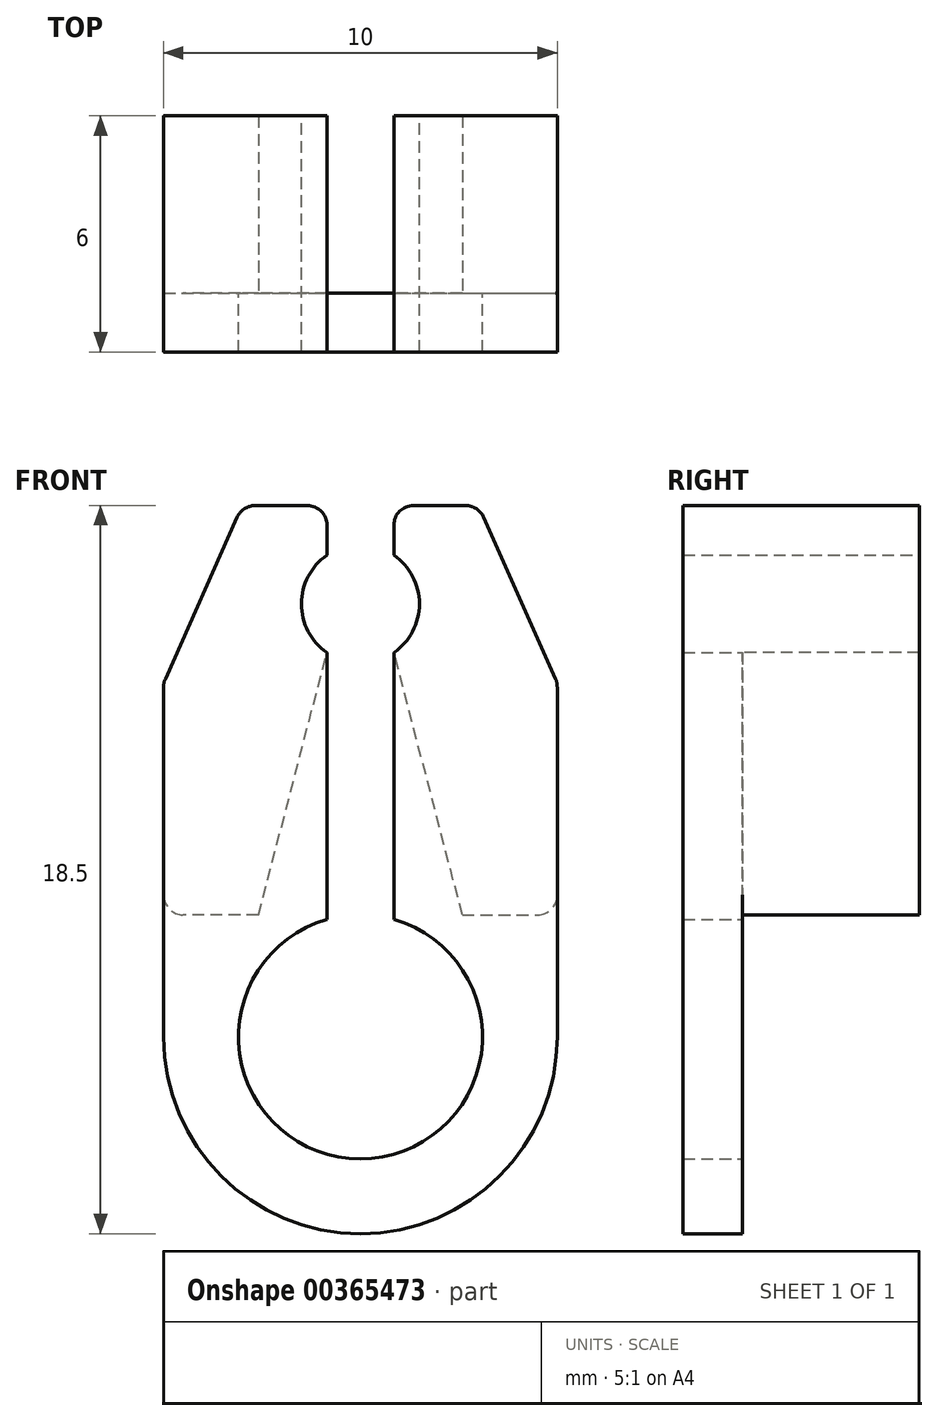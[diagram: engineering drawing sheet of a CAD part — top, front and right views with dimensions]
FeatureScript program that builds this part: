
annotation { "Feature Type Name" : "Feature", "Feature Type Description" : "" }
export const myFeature = defineFeature(function(context is Context, id is Id, definition is map)
    precondition{}
    {
        {
            var Q0;
            Q0=qCreatedBy(makeId("Front.planeOp"),FACE);
            var sketch = newSketch(context, id + "F0", { "sketchPlane" : qUnion([Q0])});
            skArc(sketch, "E0", {"start": v(-0.85, 2.98) * mm, "mid": v(0, -3.1) * mm, "end": v(0.85, 2.98) * mm});
            skArc(sketch, "E1", {"start": v(-0.85, 12.24) * mm, "mid": v(-1.5, 11) * mm, "end": v(-0.85, 9.76) * mm});
            skLineSegment(sketch, "E2", {"start": v(0, 12.5) * mm, "end": v(0, 13.5) * mm});
            skLineSegment(sketch, "E3", {"start": v(-0.85, 13.5) * mm, "end": v(-3, 13.5) * mm});
            skLineSegment(sketch, "E4", {"start": v(-5, 0) * mm, "end": v(-5, 9) * mm});
            skLineSegment(sketch, "E5", {"start": v(-5, 9) * mm, "end": v(-3, 13.5) * mm});
            skLineSegment(sketch, "E6.MirrorCS", {"start": v(5, 0) * mm, "end": v(5, 9) * mm});
            skLineSegment(sketch, "E7.MirrorCS", {"start": v(5, 9) * mm, "end": v(3, 13.5) * mm});
            skLineSegment(sketch, "E8.MirrorCS", {"start": v(0.85, 13.5) * mm, "end": v(3, 13.5) * mm});
            skLineSegment(sketch, "E9", {"start": v(-0.85, 2.98) * mm, "end": v(-0.85, 9.76) * mm});
            skLineSegment(sketch, "E10", {"start": v(0.85, 13.5) * mm, "end": v(0.85, 12.24) * mm});
            skArc(sketch, "E11.trimOffspring", {"start": v(-5, 0) * mm, "mid": v(0, -5) * mm, "end": v(5, 0) * mm});
            skPoint(sketch, "E12.orphan", {"position": v(0, 13.5) * mm});
            skLineSegment(sketch, "E13.trimOffspring", {"start": v(-0.85, 12.24) * mm, "end": v(-0.85, 13.5) * mm});
            skLineSegment(sketch, "E14.trimOffspring", {"start": v(0.85, 9.76) * mm, "end": v(0.85, 2.98) * mm});
            skArc(sketch, "E15.trimOffspring", {"start": v(0.85, 9.76) * mm, "mid": v(1.5, 11) * mm, "end": v(0.85, 12.24) * mm});
            skSolve(sketch);
        }
        {
            var Q0;
            Q0 = qSketchRegion(id + "F0", true);
            extrude(context, id + "F1", {"entities" : qUnion([Q0]), "depth" : 1.5 * mm});
        }
        {
            var Q0;
            Q0=makeQuery(id+"F1.opExtrude","CAP_FACE",FACE,{"disambiguationData":[OSD([sQuery(id+"F0.wireOp",EDGE,"E0"),sQuery(id+"F0.wireOp",EDGE,"E1"),sQuery(id+"F0.wireOp",EDGE,"E3"),sQuery(id+"F0.wireOp",EDGE,"E4"),sQuery(id+"F0.wireOp",EDGE,"E5"),sQuery(id+"F0.wireOp",EDGE,"E6.MirrorCS"),sQuery(id+"F0.wireOp",EDGE,"E7.MirrorCS"),sQuery(id+"F0.wireOp",EDGE,"E8.MirrorCS"),sQuery(id+"F0.wireOp",EDGE,"E9"),sQuery(id+"F0.wireOp",EDGE,"E10"),sQuery(id+"F0.wireOp",EDGE,"E11.trimOffspring"),sQuery(id+"F0.wireOp",EDGE,"E13.trimOffspring"),sQuery(id+"F0.wireOp",EDGE,"E14.trimOffspring"),sQuery(id+"F0.wireOp",EDGE,"E15.trimOffspring")])],"isStart":true});
            var sketch = newSketch(context, id + "F2", { "sketchPlane" : qUnion([Q0])});
            skLineSegment(sketch, "E16", {"start": v(0, 0) * mm, "end": v(0, 3.1) * mm});
            skLineSegment(sketch, "E17", {"start": v(0, 3.1) * mm, "end": v(0, 6.1) * mm});
            skLineSegment(sketch, "E18", {"start": v(2.6, 3.1) * mm, "end": v(5, 3.1) * mm});
            skPoint(sketch, "E19.orphan", {"position": v(-3.4, 0) * mm});
            skPoint(sketch, "E20.end.orphan", {"position": v(3.4, 0) * mm});
            skLineSegment(sketch, "E21", {"start": v(2.6, 3.1) * mm, "end": v(0.85, 9.76) * mm});
            skLineSegment(sketch, "E22", {"start": v(0.85, 13.5) * mm, "end": v(3, 13.5) * mm});
            skLineSegment(sketch, "E23", {"start": v(3, 13.5) * mm, "end": v(5, 9) * mm});
            skLineSegment(sketch, "E24", {"start": v(5, 9) * mm, "end": v(5, 3.1) * mm});
            skLineSegment(sketch, "E25", {"start": v(0.85, 13.5) * mm, "end": v(0.85, 12.24) * mm});
            skArc(sketch, "E26", {"start": v(0.85, 9.76) * mm, "mid": v(1.5, 11) * mm, "end": v(0.85, 12.24) * mm});
            skLineSegment(sketch, "E27.MirrorCS", {"start": v(-2.6, 3.1) * mm, "end": v(-0.85, 9.76) * mm});
            skLineSegment(sketch, "E28.MirrorCS", {"start": v(-2.6, 3.1) * mm, "end": v(-5, 3.1) * mm});
            skLineSegment(sketch, "E29.MirrorCS", {"start": v(-5, 9) * mm, "end": v(-5, 3.1) * mm});
            skLineSegment(sketch, "E30.MirrorCS", {"start": v(-3, 13.5) * mm, "end": v(-5, 9) * mm});
            skArc(sketch, "E31.MirrorCS", {"start": v(-0.85, 9.76) * mm, "mid": v(-1.5, 11) * mm, "end": v(-0.85, 12.24) * mm});
            skLineSegment(sketch, "E32.MirrorCS", {"start": v(-0.85, 13.5) * mm, "end": v(-0.85, 12.24) * mm});
            skLineSegment(sketch, "E33.MirrorCS", {"start": v(-0.85, 13.5) * mm, "end": v(-3, 13.5) * mm});
            skSolve(sketch);
        }
        {
            var Q0;
            Q0 = qSketchRegion(id + "F2", true);
            extrude(context, id + "F3", {"entities" : qUnion([Q0]), "operationType" : NewBodyOperationType.ADD, "depth" : 4.5 * mm});
        }
        {
            var Q0;
            Q0=makeQuery(id+"F3.boolean.opBoolean","MERGE",EDGE,{"derivedFrom":[makeQuery(id+"F1.opExtrude","SWEPT_EDGE",EDGE,{"disambiguationData":[OSD([sQuery(id+"F0.wireOp",EDGE,"E7.MirrorCS"),sQuery(id+"F0.wireOp",EDGE,"E8.MirrorCS")])]}),makeQuery(id+"F3.opExtrude","SWEPT_EDGE",EDGE,{"disambiguationData":[OSD([sQuery(id+"F2.wireOp",EDGE,"E30.MirrorCS"),sQuery(id+"F2.wireOp",EDGE,"E33.MirrorCS")])]})]});
            var Q1;
            Q1=makeQuery(id+"F3.boolean.opBoolean","MERGE",EDGE,{"derivedFrom":[makeQuery(id+"F1.opExtrude","SWEPT_EDGE",EDGE,{"disambiguationData":[OSD([sQuery(id+"F0.wireOp",EDGE,"E6.MirrorCS"),sQuery(id+"F0.wireOp",EDGE,"E7.MirrorCS")])]}),makeQuery(id+"F3.opExtrude","SWEPT_EDGE",EDGE,{"disambiguationData":[OSD([sQuery(id+"F2.wireOp",EDGE,"E29.MirrorCS"),sQuery(id+"F2.wireOp",EDGE,"E30.MirrorCS")])]})]});
            var Q2;
            Q2=makeQuery(id+"F3.boolean.opBoolean","MERGE",EDGE,{"derivedFrom":[makeQuery(id+"F1.opExtrude","SWEPT_EDGE",EDGE,{"disambiguationData":[OSD([sQuery(id+"F0.wireOp",EDGE,"E3"),sQuery(id+"F0.wireOp",EDGE,"E5")])]}),makeQuery(id+"F3.opExtrude","SWEPT_EDGE",EDGE,{"disambiguationData":[OSD([sQuery(id+"F2.wireOp",EDGE,"E22"),sQuery(id+"F2.wireOp",EDGE,"E23")])]})]});
            var Q3;
            Q3=makeQuery(id+"F3.boolean.opBoolean","MERGE",EDGE,{"derivedFrom":[makeQuery(id+"F1.opExtrude","SWEPT_EDGE",EDGE,{"disambiguationData":[OSD([sQuery(id+"F0.wireOp",EDGE,"E4"),sQuery(id+"F0.wireOp",EDGE,"E5")])]}),makeQuery(id+"F3.opExtrude","SWEPT_EDGE",EDGE,{"disambiguationData":[OSD([sQuery(id+"F2.wireOp",EDGE,"E23"),sQuery(id+"F2.wireOp",EDGE,"E24")])]})]});
            var Q4;
            Q4=makeQuery(id+"F3.boolean.opBoolean","MERGE",EDGE,{"derivedFrom":[makeQuery(id+"F1.opExtrude","SWEPT_EDGE",EDGE,{"disambiguationData":[OSD([sQuery(id+"F0.wireOp",EDGE,"E8.MirrorCS"),sQuery(id+"F0.wireOp",EDGE,"E10")])]}),makeQuery(id+"F3.opExtrude","SWEPT_EDGE",EDGE,{"disambiguationData":[OSD([sQuery(id+"F2.wireOp",EDGE,"E32.MirrorCS"),sQuery(id+"F2.wireOp",EDGE,"E33.MirrorCS")])]})]});
            var Q5;
            Q5=makeQuery(id+"F3.boolean.opBoolean","MERGE",EDGE,{"derivedFrom":[makeQuery(id+"F1.opExtrude","SWEPT_EDGE",EDGE,{"disambiguationData":[OSD([sQuery(id+"F0.wireOp",EDGE,"E3"),sQuery(id+"F0.wireOp",EDGE,"E13.trimOffspring")])]}),makeQuery(id+"F3.opExtrude","SWEPT_EDGE",EDGE,{"disambiguationData":[OSD([sQuery(id+"F2.wireOp",EDGE,"E22"),sQuery(id+"F2.wireOp",EDGE,"E25")])]})]});
            var Q6;
            Q6=makeQuery(id+"F3.opExtrude","SWEPT_EDGE",EDGE,{"disambiguationData":[OSD([sQuery(id+"F0.wireOp",EDGE,"E6.MirrorCS"),sQuery(id+"F2.wireOp",EDGE,"E28.MirrorCS"),sQuery(id+"F2.wireOp",EDGE,"E29.MirrorCS")])]});
            var Q7;
            Q7=makeQuery(id+"F3.opExtrude","SWEPT_EDGE",EDGE,{"disambiguationData":[OSD([sQuery(id+"F0.wireOp",EDGE,"E4"),sQuery(id+"F2.wireOp",EDGE,"E18"),sQuery(id+"F2.wireOp",EDGE,"E24")])]});
            fillet(context, id + "F4", {"entities" : qUnion([Q0, Q1, Q2, Q3, Q4, Q5, Q6, Q7]), "radius" : 0.5 * mm, "tangentPropagation" : true, "allowEdgeOverflow" : false});
        }
    });
